# Revit family: Cruzer
name_source: partatom
category: Lighting Fixtures
units: mm (PartAtom-declared; Revit-internal decimal feet)

## family parameters
Cut with Voids When Loaded = No
Host = Face
Light Source = Yes
OmniClass Number = 23.80.70.14.21
OmniClass Title = Street and Roadway Lighting
Part Type = Normal
Room Calculation Point = No
Round Connector Dimension = Use Diameter
Shared = No

## types (12) — shared parameters
Apparent Load = 0 VA
Color Filter = 16777215
Default Elevation = 48.00"
Description = Cruzer Area Luminaire
Dimming Lamp Color Temperature Shift = <None>
Emit Shape Visible in Rendering = No
Emit from Rectangle Length = 10.00"
Emit from Rectangle Width = 10.00"
Glass = Glass
Input Wattage = 27 W
Lamp = LED
Load Classification = Lighting
Manufacturer = Beacon Products
Model = CRUZER
Mounting Option = AM
Photometric Web File = CRZ-24NB-27-3K-T2.ies
Tilt Angle = 90.00°
URL = https://www.currentlighting.com
Voltage = 120 V
Wattage Comments = 27,55,80,110 & 136 Watts

## per-type parameters (varying)
| type | Assembly Code | Product Material |
| Basic Black Textured |  | Paint - Basic Black Textured |
| Black Matte Textured |  | Paint - Black Matte Textured |
| Bronze Textured |  | Paint -  Bronze Textured |
| Dark Bronze Textured |  | Paint -  Dark Bronze Textured |
| Dark Platinum Smooth |  | Paint - Dark Platinum Smooth |
| Gray Smooth |  | Paint - Gray Smooth |
| Green Textured |  | Paint - Green Textured |
| Metallic Bronze Textured |  | Paint - Metallic Bronze Textured |
| Metallic Silver Textured |  | Paint -Metallic Silver Textured |
| Metallic Titanium Textured |  | Paint - Metallic Titanium Textured |
| Old World Iron |  | Paint - Old World Iron |
| White Texture | D5020280 | Paint - White Texture |

## geometry (parser evidence)
native form markers: Sweep x11
no freeform markers — native parametric forms only
